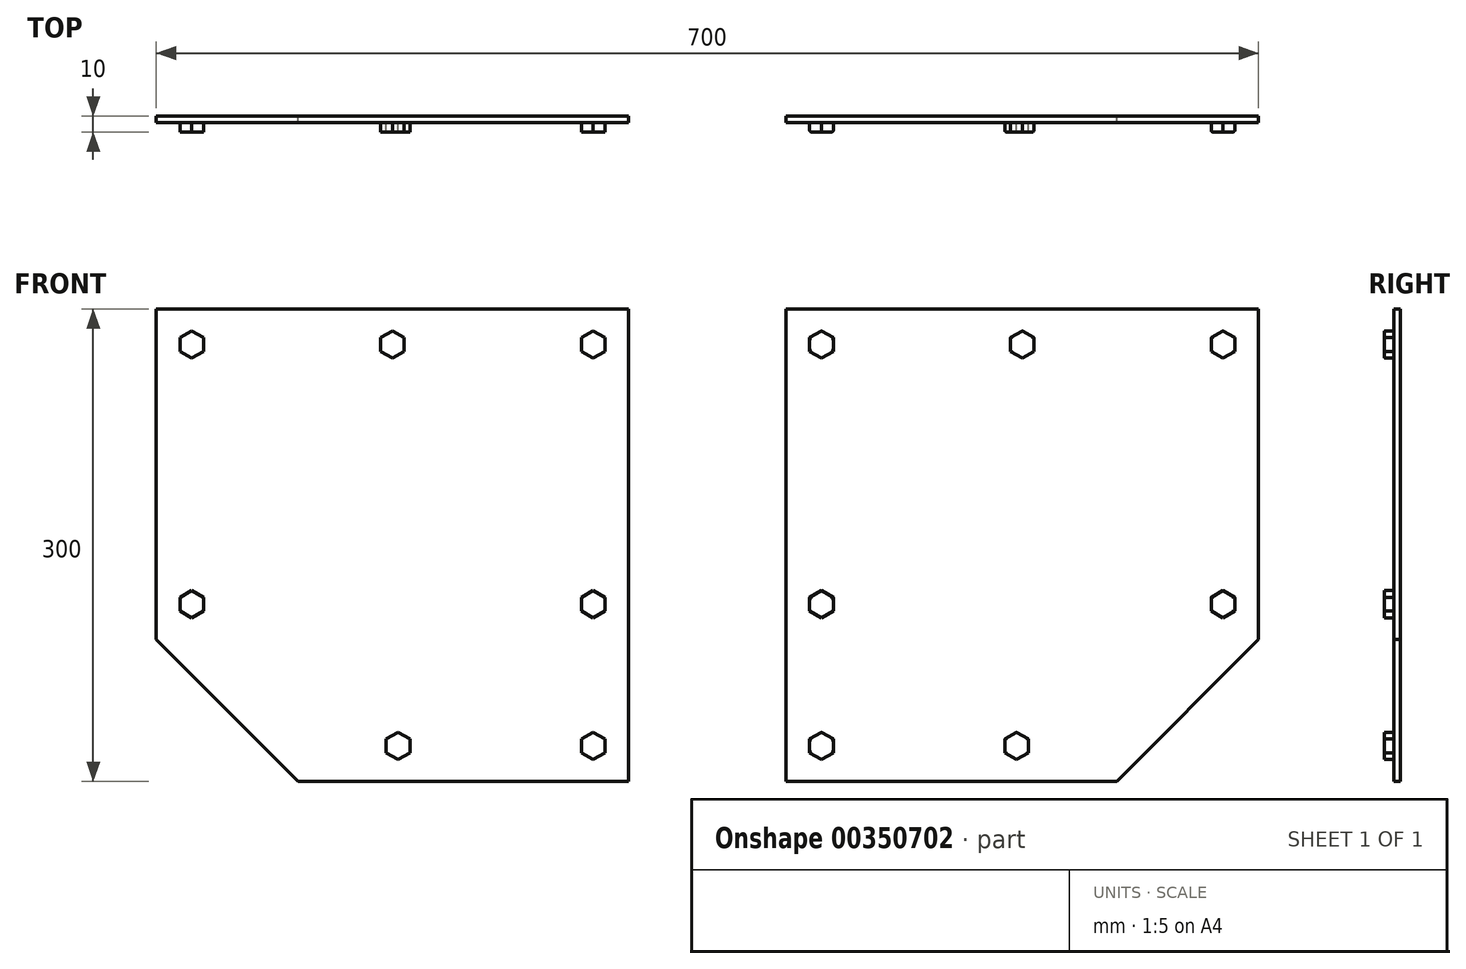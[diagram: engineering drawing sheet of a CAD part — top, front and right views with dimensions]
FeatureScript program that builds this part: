
annotation { "Feature Type Name" : "Feature", "Feature Type Description" : "" }
export const myFeature = defineFeature(function(context is Context, id is Id, definition is map)
    precondition{}
    {
        {
            var Q0;
            Q0=qCreatedBy(makeId("Front.planeOp"),FACE);
            var sketch = newSketch(context, id + "F0", { "sketchPlane" : qUnion([Q0])});
            skLineSegment(sketch, "E0", {"start": v(50, 0) * mm, "end": v(50, 300) * mm});
            skLineSegment(sketch, "E1", {"start": v(50, 300) * mm, "end": v(350, 300) * mm});
            skLineSegment(sketch, "E2", {"start": v(50, 0) * mm, "end": v(260, 0) * mm});
            skLineSegment(sketch, "E3", {"start": v(350, 300) * mm, "end": v(350, 90) * mm});
            skLineSegment(sketch, "E4", {"start": v(350, 90) * mm, "end": v(260, 0) * mm});
            skLineSegment(sketch, "E5.MirrorCS", {"start": v(-350, 90) * mm, "end": v(-260, 0) * mm});
            skLineSegment(sketch, "E6.MirrorCS", {"start": v(-350, 300) * mm, "end": v(-350, 90) * mm});
            skLineSegment(sketch, "E7.MirrorCS", {"start": v(-50, 0) * mm, "end": v(-260, 0) * mm});
            skLineSegment(sketch, "E8.MirrorCS", {"start": v(-50, 0) * mm, "end": v(-50, 300) * mm});
            skLineSegment(sketch, "E9.MirrorCS", {"start": v(-50, 300) * mm, "end": v(-350, 300) * mm});
            skSolve(sketch);
        }
        {
            var Q0;
            Q0 = qSketchRegion(id + "F0", true);
            extrude(context, id + "F1", {"entities" : qUnion([Q0]), "depth" : 4 * mm});
        }
        {
            var Q0;
            Q0=makeQuery(id+"F1.opExtrude","CAP_FACE",FACE,{"disambiguationData":[OSD([sQuery(id+"F0.wireOp",EDGE,"E0"),sQuery(id+"F0.wireOp",EDGE,"E1"),sQuery(id+"F0.wireOp",EDGE,"E2"),sQuery(id+"F0.wireOp",EDGE,"E3"),sQuery(id+"F0.wireOp",EDGE,"E4")])],"isStart":false});
            var sketch = newSketch(context, id + "F2", { "sketchPlane" : qUnion([Q0])});
            skCircle(sketch, "E10.cCircle", {"center": v(72.5, 277.5) * mm, "radius": 7.5 * mm, "construction": true});
            skLineSegment(sketch, "E10.0", {"start": v(80, 273.17) * mm, "end": v(72.5, 268.84) * mm});
            skLineSegment(sketch, "E10.1", {"start": v(72.5, 268.84) * mm, "end": v(65, 273.17) * mm});
            skLineSegment(sketch, "E10.2", {"start": v(65, 273.17) * mm, "end": v(65, 281.83) * mm});
            skLineSegment(sketch, "E10.3", {"start": v(65, 281.83) * mm, "end": v(72.5, 286.16) * mm});
            skLineSegment(sketch, "E10.4", {"start": v(72.5, 286.16) * mm, "end": v(80, 281.83) * mm});
            skLineSegment(sketch, "E10.5", {"start": v(80, 281.83) * mm, "end": v(80, 273.17) * mm});
            skPoint(sketch, "E10.0.midPoint", {"position": v(76.25, 271) * mm});
            skCircle(sketch, "E11.cCircle", {"center": v(200, 277.5) * mm, "radius": 7.5 * mm, "construction": true});
            skLineSegment(sketch, "E11.0", {"start": v(207.5, 273.17) * mm, "end": v(200, 268.84) * mm});
            skLineSegment(sketch, "E11.1", {"start": v(200, 268.84) * mm, "end": v(192.5, 273.17) * mm});
            skLineSegment(sketch, "E11.2", {"start": v(192.5, 273.17) * mm, "end": v(192.5, 281.83) * mm});
            skLineSegment(sketch, "E11.3", {"start": v(192.5, 281.83) * mm, "end": v(200, 286.16) * mm});
            skLineSegment(sketch, "E11.4", {"start": v(200, 286.16) * mm, "end": v(207.5, 281.83) * mm});
            skLineSegment(sketch, "E11.5", {"start": v(207.5, 281.83) * mm, "end": v(207.5, 273.17) * mm});
            skPoint(sketch, "E11.0.midPoint", {"position": v(203.75, 271) * mm});
            skPoint(sketch, "E12", {"position": v(80, 277.5) * mm});
            skCircle(sketch, "E13.cCircle", {"center": v(327.5, 277.5) * mm, "radius": 7.5 * mm, "construction": true});
            skLineSegment(sketch, "E13.0", {"start": v(335, 273.17) * mm, "end": v(327.5, 268.84) * mm});
            skLineSegment(sketch, "E13.1", {"start": v(327.5, 268.84) * mm, "end": v(320, 273.17) * mm});
            skLineSegment(sketch, "E13.2", {"start": v(320, 273.17) * mm, "end": v(320, 281.83) * mm});
            skLineSegment(sketch, "E13.3", {"start": v(320, 281.83) * mm, "end": v(327.5, 286.16) * mm});
            skLineSegment(sketch, "E13.4", {"start": v(327.5, 286.16) * mm, "end": v(335, 281.83) * mm});
            skLineSegment(sketch, "E13.5", {"start": v(335, 281.83) * mm, "end": v(335, 273.17) * mm});
            skPoint(sketch, "E13.0.midPoint", {"position": v(331.25, 271) * mm});
            skCircle(sketch, "E14.cCircle", {"center": v(327.5, 112.5) * mm, "radius": 7.5 * mm, "construction": true});
            skLineSegment(sketch, "E14.0", {"start": v(335, 108.17) * mm, "end": v(327.5, 103.84) * mm});
            skLineSegment(sketch, "E14.1", {"start": v(327.5, 103.84) * mm, "end": v(320, 108.17) * mm});
            skLineSegment(sketch, "E14.2", {"start": v(320, 108.17) * mm, "end": v(320, 116.83) * mm});
            skLineSegment(sketch, "E14.3", {"start": v(320, 116.83) * mm, "end": v(327.5, 121.16) * mm});
            skLineSegment(sketch, "E14.4", {"start": v(327.5, 121.16) * mm, "end": v(335, 116.83) * mm});
            skLineSegment(sketch, "E14.5", {"start": v(335, 116.83) * mm, "end": v(335, 108.17) * mm});
            skPoint(sketch, "E14.0.midPoint", {"position": v(331.25, 106) * mm});
            skCircle(sketch, "E15.cCircle", {"center": v(72.5, 112.5) * mm, "radius": 7.5 * mm, "construction": true});
            skLineSegment(sketch, "E15.0", {"start": v(80, 108.17) * mm, "end": v(72.5, 103.84) * mm});
            skLineSegment(sketch, "E15.1", {"start": v(72.5, 103.84) * mm, "end": v(65, 108.17) * mm});
            skLineSegment(sketch, "E15.2", {"start": v(65, 108.17) * mm, "end": v(65, 116.83) * mm});
            skLineSegment(sketch, "E15.3", {"start": v(65, 116.83) * mm, "end": v(72.5, 121.16) * mm});
            skLineSegment(sketch, "E15.4", {"start": v(72.5, 121.16) * mm, "end": v(80, 116.83) * mm});
            skLineSegment(sketch, "E15.5", {"start": v(80, 116.83) * mm, "end": v(80, 108.17) * mm});
            skPoint(sketch, "E15.0.midPoint", {"position": v(76.25, 106) * mm});
            skPoint(sketch, "E16", {"position": v(320, 112.5) * mm});
            skCircle(sketch, "E17.cCircle", {"center": v(72.5, 22.5) * mm, "radius": 7.5 * mm, "construction": true});
            skLineSegment(sketch, "E17.0", {"start": v(80, 18.17) * mm, "end": v(72.5, 13.84) * mm});
            skLineSegment(sketch, "E17.1", {"start": v(72.5, 13.84) * mm, "end": v(65, 18.17) * mm});
            skLineSegment(sketch, "E17.2", {"start": v(65, 18.17) * mm, "end": v(65, 26.83) * mm});
            skLineSegment(sketch, "E17.3", {"start": v(65, 26.83) * mm, "end": v(72.5, 31.16) * mm});
            skLineSegment(sketch, "E17.4", {"start": v(72.5, 31.16) * mm, "end": v(80, 26.83) * mm});
            skLineSegment(sketch, "E17.5", {"start": v(80, 26.83) * mm, "end": v(80, 18.17) * mm});
            skPoint(sketch, "E17.0.midPoint", {"position": v(76.25, 16) * mm});
            skCircle(sketch, "E18.cCircle", {"center": v(196.42, 22.5) * mm, "radius": 7.5 * mm, "construction": true});
            skLineSegment(sketch, "E18.0", {"start": v(203.92, 18.17) * mm, "end": v(196.42, 13.84) * mm});
            skLineSegment(sketch, "E18.1", {"start": v(196.42, 13.84) * mm, "end": v(188.92, 18.17) * mm});
            skLineSegment(sketch, "E18.2", {"start": v(188.92, 18.17) * mm, "end": v(188.92, 26.83) * mm});
            skLineSegment(sketch, "E18.3", {"start": v(188.92, 26.83) * mm, "end": v(196.42, 31.16) * mm});
            skLineSegment(sketch, "E18.4", {"start": v(196.42, 31.16) * mm, "end": v(203.92, 26.83) * mm});
            skLineSegment(sketch, "E18.5", {"start": v(203.92, 26.83) * mm, "end": v(203.92, 18.17) * mm});
            skPoint(sketch, "E18.0.midPoint", {"position": v(200.17, 16) * mm});
            skPoint(sketch, "E19", {"position": v(80, 22.5) * mm});
            skLineSegment(sketch, "E20.MirrorCS", {"start": v(-320, 108.17) * mm, "end": v(-320, 116.83) * mm});
            skLineSegment(sketch, "E21.MirrorCS", {"start": v(-335, 108.17) * mm, "end": v(-327.5, 103.84) * mm});
            skLineSegment(sketch, "E22.MirrorCS", {"start": v(-335, 116.83) * mm, "end": v(-335, 108.17) * mm});
            skLineSegment(sketch, "E23.MirrorCS", {"start": v(-72.5, 103.84) * mm, "end": v(-65, 108.17) * mm});
            skLineSegment(sketch, "E24.MirrorCS", {"start": v(-203.92, 18.17) * mm, "end": v(-196.42, 13.84) * mm});
            skLineSegment(sketch, "E25.MirrorCS", {"start": v(-65, 108.17) * mm, "end": v(-65, 116.83) * mm});
            skLineSegment(sketch, "E26.MirrorCS", {"start": v(-207.5, 281.83) * mm, "end": v(-207.5, 273.17) * mm});
            skLineSegment(sketch, "E27.MirrorCS", {"start": v(-65, 273.17) * mm, "end": v(-65, 281.83) * mm});
            skLineSegment(sketch, "E28.MirrorCS", {"start": v(-72.5, 268.84) * mm, "end": v(-65, 273.17) * mm});
            skLineSegment(sketch, "E29.MirrorCS", {"start": v(-72.5, 286.16) * mm, "end": v(-80, 281.83) * mm});
            skLineSegment(sketch, "E30.MirrorCS", {"start": v(-335, 281.83) * mm, "end": v(-335, 273.17) * mm});
            skLineSegment(sketch, "E31.MirrorCS", {"start": v(-196.42, 31.16) * mm, "end": v(-203.92, 26.83) * mm});
            skLineSegment(sketch, "E32.MirrorCS", {"start": v(-335, 273.17) * mm, "end": v(-327.5, 268.84) * mm});
            skLineSegment(sketch, "E33.MirrorCS", {"start": v(-80, 273.17) * mm, "end": v(-72.5, 268.84) * mm});
            skLineSegment(sketch, "E34.MirrorCS", {"start": v(-188.92, 26.83) * mm, "end": v(-196.42, 31.16) * mm});
            skLineSegment(sketch, "E35.MirrorCS", {"start": v(-320, 273.17) * mm, "end": v(-320, 281.83) * mm});
            skLineSegment(sketch, "E36.MirrorCS", {"start": v(-65, 116.83) * mm, "end": v(-72.5, 121.16) * mm});
            skLineSegment(sketch, "E37.MirrorCS", {"start": v(-65, 26.83) * mm, "end": v(-72.5, 31.16) * mm});
            skLineSegment(sketch, "E38.MirrorCS", {"start": v(-203.92, 26.83) * mm, "end": v(-203.92, 18.17) * mm});
            skLineSegment(sketch, "E39.MirrorCS", {"start": v(-200, 268.84) * mm, "end": v(-192.5, 273.17) * mm});
            skLineSegment(sketch, "E40.MirrorCS", {"start": v(-207.5, 273.17) * mm, "end": v(-200, 268.84) * mm});
            skLineSegment(sketch, "E41.MirrorCS", {"start": v(-80, 108.17) * mm, "end": v(-72.5, 103.84) * mm});
            skLineSegment(sketch, "E42.MirrorCS", {"start": v(-72.5, 13.84) * mm, "end": v(-65, 18.17) * mm});
            skLineSegment(sketch, "E43.MirrorCS", {"start": v(-327.5, 268.84) * mm, "end": v(-320, 273.17) * mm});
            skLineSegment(sketch, "E44.MirrorCS", {"start": v(-200, 286.16) * mm, "end": v(-207.5, 281.83) * mm});
            skLineSegment(sketch, "E45.MirrorCS", {"start": v(-72.5, 31.16) * mm, "end": v(-80, 26.83) * mm});
            skLineSegment(sketch, "E46.MirrorCS", {"start": v(-80, 18.17) * mm, "end": v(-72.5, 13.84) * mm});
            skLineSegment(sketch, "E47.MirrorCS", {"start": v(-327.5, 103.84) * mm, "end": v(-320, 108.17) * mm});
            skLineSegment(sketch, "E48.MirrorCS", {"start": v(-80, 116.83) * mm, "end": v(-80, 108.17) * mm});
            skLineSegment(sketch, "E49.MirrorCS", {"start": v(-196.42, 13.84) * mm, "end": v(-188.92, 18.17) * mm});
            skLineSegment(sketch, "E50.MirrorCS", {"start": v(-188.92, 18.17) * mm, "end": v(-188.92, 26.83) * mm});
            skLineSegment(sketch, "E51.MirrorCS", {"start": v(-320, 116.83) * mm, "end": v(-327.5, 121.16) * mm});
            skLineSegment(sketch, "E52.MirrorCS", {"start": v(-192.5, 281.83) * mm, "end": v(-200, 286.16) * mm});
            skLineSegment(sketch, "E53.MirrorCS", {"start": v(-80, 26.83) * mm, "end": v(-80, 18.17) * mm});
            skLineSegment(sketch, "E54.MirrorCS", {"start": v(-320, 281.83) * mm, "end": v(-327.5, 286.16) * mm});
            skLineSegment(sketch, "E55.MirrorCS", {"start": v(-327.5, 121.16) * mm, "end": v(-335, 116.83) * mm});
            skLineSegment(sketch, "E56.MirrorCS", {"start": v(-327.5, 286.16) * mm, "end": v(-335, 281.83) * mm});
            skLineSegment(sketch, "E57.MirrorCS", {"start": v(-80, 281.83) * mm, "end": v(-80, 273.17) * mm});
            skCircle(sketch, "E58.MirrorC", {"center": v(-327.5, 112.5) * mm, "radius": 7.5 * mm, "construction": true});
            skCircle(sketch, "E59.MirrorC", {"center": v(-327.5, 277.5) * mm, "radius": 7.5 * mm, "construction": true});
            skLineSegment(sketch, "E60.MirrorCS", {"start": v(-72.5, 121.16) * mm, "end": v(-80, 116.83) * mm});
            skCircle(sketch, "E61.MirrorC", {"center": v(-196.42, 22.5) * mm, "radius": 7.5 * mm, "construction": true});
            skLineSegment(sketch, "E62.MirrorCS", {"start": v(-192.5, 273.17) * mm, "end": v(-192.5, 281.83) * mm});
            skCircle(sketch, "E63.MirrorC", {"center": v(-72.5, 277.5) * mm, "radius": 7.5 * mm, "construction": true});
            skLineSegment(sketch, "E64.MirrorCS", {"start": v(-65, 18.17) * mm, "end": v(-65, 26.83) * mm});
            skLineSegment(sketch, "E65.MirrorCS", {"start": v(-65, 281.83) * mm, "end": v(-72.5, 286.16) * mm});
            skCircle(sketch, "E66.MirrorC", {"center": v(-200, 277.5) * mm, "radius": 7.5 * mm, "construction": true});
            skCircle(sketch, "E67.MirrorC", {"center": v(-72.5, 112.5) * mm, "radius": 7.5 * mm, "construction": true});
            skCircle(sketch, "E68.MirrorC", {"center": v(-72.5, 22.5) * mm, "radius": 7.5 * mm, "construction": true});
            skPoint(sketch, "E69.MirrorP", {"position": v(-76.25, 106) * mm});
            skPoint(sketch, "E70.MirrorP", {"position": v(-76.25, 16) * mm});
            skPoint(sketch, "E71.MirrorP", {"position": v(-200.17, 16) * mm});
            skPoint(sketch, "E72.MirrorP", {"position": v(-320, 112.5) * mm});
            skPoint(sketch, "E73.MirrorP", {"position": v(-80, 277.5) * mm});
            skPoint(sketch, "E74.MirrorP", {"position": v(-80, 22.5) * mm});
            skPoint(sketch, "E75.MirrorP", {"position": v(-203.75, 271) * mm});
            skPoint(sketch, "E76.MirrorP", {"position": v(-331.25, 106) * mm});
            skPoint(sketch, "E77.MirrorP", {"position": v(-331.25, 271) * mm});
            skPoint(sketch, "E78.MirrorP", {"position": v(-76.25, 271) * mm});
            skSolve(sketch);
        }
        {
            var Q0;
            Q0 = qSketchRegion(id + "F2", true);
            extrude(context, id + "F3", {"entities" : qUnion([Q0]), "operationType" : NewBodyOperationType.ADD, "depth" : 6 * mm});
        }
        {
            var Q0;
            Q0=makeQuery(id+"F3.opExtrude","CAP_FACE",FACE,{"disambiguationData":[OSD([sQuery(id+"F2.wireOp",EDGE,"E10.0"),sQuery(id+"F2.wireOp",EDGE,"E10.1"),sQuery(id+"F2.wireOp",EDGE,"E10.2"),sQuery(id+"F2.wireOp",EDGE,"E10.3"),sQuery(id+"F2.wireOp",EDGE,"E10.4"),sQuery(id+"F2.wireOp",EDGE,"E10.5")])],"isStart":false});
            var Q1;
            Q1=makeQuery(id+"F3.opExtrude","CAP_FACE",FACE,{"disambiguationData":[OSD([sQuery(id+"F2.wireOp",EDGE,"E11.0"),sQuery(id+"F2.wireOp",EDGE,"E11.1"),sQuery(id+"F2.wireOp",EDGE,"E11.2"),sQuery(id+"F2.wireOp",EDGE,"E11.3"),sQuery(id+"F2.wireOp",EDGE,"E11.4"),sQuery(id+"F2.wireOp",EDGE,"E11.5")])],"isStart":false});
            var Q2;
            Q2=makeQuery(id+"F3.opExtrude","CAP_FACE",FACE,{"disambiguationData":[OSD([sQuery(id+"F2.wireOp",EDGE,"E13.0"),sQuery(id+"F2.wireOp",EDGE,"E13.1"),sQuery(id+"F2.wireOp",EDGE,"E13.2"),sQuery(id+"F2.wireOp",EDGE,"E13.3"),sQuery(id+"F2.wireOp",EDGE,"E13.4"),sQuery(id+"F2.wireOp",EDGE,"E13.5")])],"isStart":false});
            var Q3;
            Q3=makeQuery(id+"F3.opExtrude","CAP_FACE",FACE,{"disambiguationData":[OSD([sQuery(id+"F2.wireOp",EDGE,"E15.0"),sQuery(id+"F2.wireOp",EDGE,"E15.1"),sQuery(id+"F2.wireOp",EDGE,"E15.2"),sQuery(id+"F2.wireOp",EDGE,"E15.3"),sQuery(id+"F2.wireOp",EDGE,"E15.4"),sQuery(id+"F2.wireOp",EDGE,"E15.5")])],"isStart":false});
            var Q4;
            Q4=makeQuery(id+"F3.opExtrude","CAP_FACE",FACE,{"disambiguationData":[OSD([sQuery(id+"F2.wireOp",EDGE,"E14.0"),sQuery(id+"F2.wireOp",EDGE,"E14.1"),sQuery(id+"F2.wireOp",EDGE,"E14.2"),sQuery(id+"F2.wireOp",EDGE,"E14.3"),sQuery(id+"F2.wireOp",EDGE,"E14.4"),sQuery(id+"F2.wireOp",EDGE,"E14.5")])],"isStart":false});
            var Q5;
            Q5=makeQuery(id+"F3.opExtrude","CAP_FACE",FACE,{"disambiguationData":[OSD([sQuery(id+"F2.wireOp",EDGE,"E18.0"),sQuery(id+"F2.wireOp",EDGE,"E18.1"),sQuery(id+"F2.wireOp",EDGE,"E18.2"),sQuery(id+"F2.wireOp",EDGE,"E18.3"),sQuery(id+"F2.wireOp",EDGE,"E18.4"),sQuery(id+"F2.wireOp",EDGE,"E18.5")])],"isStart":false});
            var Q6;
            Q6=makeQuery(id+"F3.opExtrude","CAP_FACE",FACE,{"disambiguationData":[OSD([sQuery(id+"F2.wireOp",EDGE,"E17.0"),sQuery(id+"F2.wireOp",EDGE,"E17.1"),sQuery(id+"F2.wireOp",EDGE,"E17.2"),sQuery(id+"F2.wireOp",EDGE,"E17.3"),sQuery(id+"F2.wireOp",EDGE,"E17.4"),sQuery(id+"F2.wireOp",EDGE,"E17.5")])],"isStart":false});
            fillet(context, id + "F4", {"entities" : qUnion([Q0, Q1, Q2, Q3, Q4, Q5, Q6]), "radius" : 1 * mm, "tangentPropagation" : true, "allowEdgeOverflow" : false});
        }
    });
